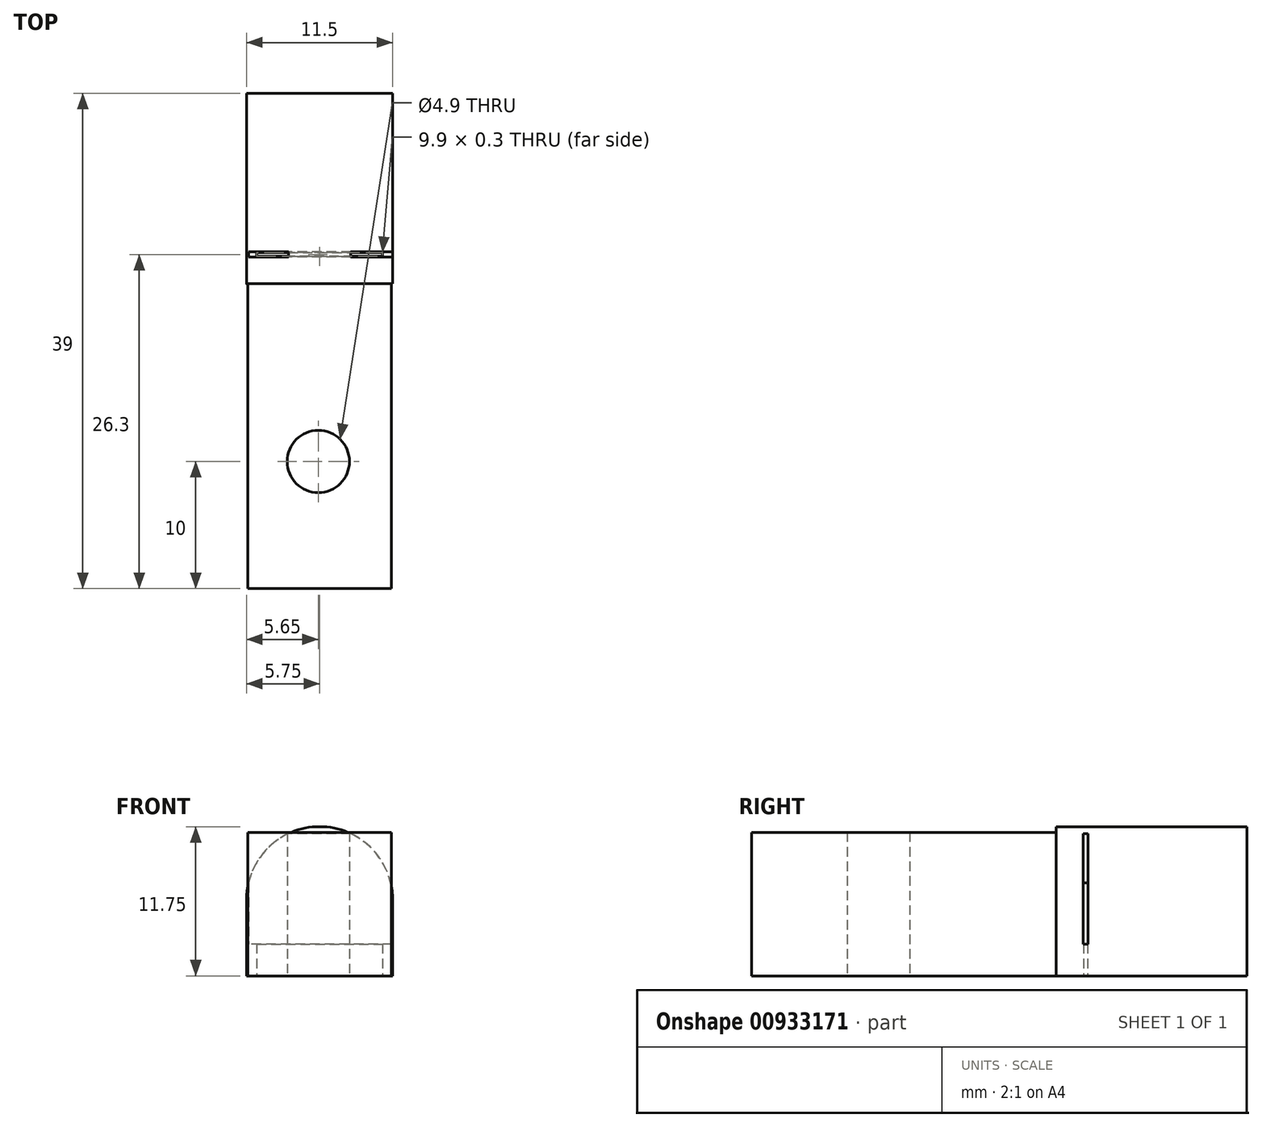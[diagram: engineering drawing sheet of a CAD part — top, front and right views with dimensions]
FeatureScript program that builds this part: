
annotation { "Feature Type Name" : "Feature", "Feature Type Description" : "" }
export const myFeature = defineFeature(function(context is Context, id is Id, definition is map)
    precondition{}
    {
        {
            var Q0;
            Q0=qCreatedBy(makeId("Front.planeOp"),FACE);
            var sketch = newSketch(context, id + "F0", { "sketchPlane" : qUnion([Q0])});
            skLineSegment(sketch, "E0.bottom", {"start": v(0, 0) * mm, "end": v(11.5, 0) * mm});
            skLineSegment(sketch, "E0.top", {"start": v(0, 6) * mm, "end": v(11.5, 6) * mm});
            skLineSegment(sketch, "E0.left", {"start": v(0, 0) * mm, "end": v(0, 6) * mm});
            skLineSegment(sketch, "E0.right", {"start": v(11.5, 0) * mm, "end": v(11.5, 6) * mm});
            skArc(sketch, "E1", {"start": v(0, 6) * mm, "mid": v(5.75, 11.75) * mm, "end": v(11.5, 6) * mm});
            skSolve(sketch);
        }
        {
            var Q0;
            Q0=makeQuery(id+"F0.imprint","IMPRINT",FACE,{"disambiguationData":[TD([[makeQuery(id+"F0.imprint","IMPRINT",EDGE,{"derivedFrom":sQuery(id+"F0.wireOp",EDGE,"E0.top")}),1.0]])]});
            var Q1;
            Q1=makeQuery(id+"F0.imprint","IMPRINT",FACE,{"disambiguationData":[TD([[makeQuery(id+"F0.imprint","IMPRINT",EDGE,{"derivedFrom":sQuery(id+"F0.wireOp",EDGE,"E0.bottom")}),1.0]])]});
            extrude(context, id + "F1", {"entities" : qUnion([Q0, Q1]), "depth" : 15 * mm, "offsetDistance" : 25 * mm});
        }
        {
            var Q0;
            Q0=makeQuery(id+"F1.opExtrude","CAP_FACE",FACE,{"disambiguationData":[OSD([sQuery(id+"F0.wireOp",EDGE,"E0.bottom"),sQuery(id+"F0.wireOp",EDGE,"E0.left"),sQuery(id+"F0.wireOp",EDGE,"E0.right"),sQuery(id+"F0.wireOp",EDGE,"E1")])],"isStart":false});
            var sketch = newSketch(context, id + "F2", { "sketchPlane" : qUnion([Q0])});
            skLineSegment(sketch, "E2.bottom", {"start": v(11.4, 0) * mm, "end": v(0.1, 0) * mm});
            skLineSegment(sketch, "E2.top", {"start": v(11.4, 11.3) * mm, "end": v(0.1, 11.3) * mm});
            skLineSegment(sketch, "E2.left", {"start": v(11.4, 0) * mm, "end": v(11.4, 11.3) * mm});
            skLineSegment(sketch, "E2.right", {"start": v(0.1, 0) * mm, "end": v(0.1, 11.3) * mm});
            skPoint(sketch, "E2.middle", {"position": v(5.75, 5.65) * mm});
            skPoint(sketch, "E2.middle.positionSnap0", {"position": v(5.75, 0) * mm});
            skPoint(sketch, "E2.centerSnap0", {"position": v(5.75, 0) * mm});
            skSolve(sketch);
        }
        {
            var Q0;
            Q0=qSketchRegion(id+"F2",true);
            extrude(context, id + "F3", {"entities" : qUnion([Q0]), "operationType" : NewBodyOperationType.ADD, "depth" : 24 * mm, "offsetDistance" : 25 * mm});
        }
        {
            var Q0;
            Q0=makeQuery(id+"F1.opExtrude","CAP_VERTEX",VERTEX,{"disambiguationData":[OSD([sQuery(id+"F0.wireOp",EDGE,"E0.top"),sQuery(id+"F0.wireOp",EDGE,"E0.left"),sQuery(id+"F0.wireOp",EDGE,"E1")])],"isStart":true});
            var Q1;
            Q1=makeQuery(id+"F1.opExtrude","CAP_VERTEX",VERTEX,{"disambiguationData":[OSD([sQuery(id+"F0.wireOp",EDGE,"E0.top"),sQuery(id+"F0.wireOp",EDGE,"E0.left"),sQuery(id+"F0.wireOp",EDGE,"E1")])],"isStart":false});
            var Q2;
            Q2=makeQuery(id+"F1.opExtrude","CAP_VERTEX",VERTEX,{"disambiguationData":[OSD([sQuery(id+"F0.wireOp",EDGE,"E0.top"),sQuery(id+"F0.wireOp",EDGE,"E0.right"),sQuery(id+"F0.wireOp",EDGE,"E1")])],"isStart":true});
            cPlane(context, id + "F4", {"entities" : qUnion([Q0, Q1, Q2]), "cplaneType" : CPlaneType.THREE_POINT, "offset" : 25 * mm, "width" : 150 * mm, "height" : 150 * mm});
        }
        {
            var Q0;
            Q0=qCreatedBy(id+"F4.planeOp",FACE);
            var sketch = newSketch(context, id + "F5", { "sketchPlane" : qUnion([Q0])});
            skPoint(sketch, "E3.0", {"position": v(11.9, 12.7) * mm});
            skPoint(sketch, "E4.0", {"position": v(0, 9.7) * mm});
            skLineSegment(sketch, "E5", {"start": v(13.51, 12.7) * mm, "end": v(-0.54, 12.7) * mm, "construction": true});
            skLineSegment(sketch, "E6.bottom", {"start": v(12.82, 12.9) * mm, "end": v(0.15, 12.9) * mm});
            skLineSegment(sketch, "E6.top", {"start": v(12.82, 12.5) * mm, "end": v(0.15, 12.5) * mm});
            skLineSegment(sketch, "E6.left", {"start": v(12.82, 12.9) * mm, "end": v(12.82, 12.5) * mm});
            skLineSegment(sketch, "E6.right", {"start": v(0.15, 12.9) * mm, "end": v(0.15, 12.5) * mm});
            skPoint(sketch, "E6.middle", {"position": v(6.49, 12.7) * mm});
            skSolve(sketch);
        }
        {
            var Q0;
            Q0=makeQuery(id+"F5.imprint","IMPRINT",FACE,{"disambiguationData":[TD([[makeQuery(id+"F5.imprint","IMPRINT",EDGE,{"derivedFrom":sQuery(id+"F5.wireOp",EDGE,"E6.bottom")}),1.0]])]});
            extrude(context, id + "F6", {"entities" : qUnion([Q0]), "operationType" : NewBodyOperationType.REMOVE, "oppositeDirection" : true, "depth" : 5.2 * mm, "offsetDistance" : 25 * mm});
        }
        {
            var Q0;
            Q0=makeQuery(id+"F3.boolean.opBoolean","MERGE",FACE,{"derivedFrom":[makeQuery(id+"F1.opExtrude","SWEPT_FACE",FACE,{"disambiguationData":[OSD([sQuery(id+"F0.wireOp",EDGE,"E0.bottom")])]}),makeQuery(id+"F3.opExtrude","SWEPT_FACE",FACE,{"disambiguationData":[OSD([sQuery(id+"F2.wireOp",EDGE,"E2.bottom")])]})]});
            var sketch = newSketch(context, id + "F7", { "sketchPlane" : qUnion([Q0])});
            skLineSegment(sketch, "E7", {"start": v(11.5, 12.7) * mm, "end": v(0, 12.7) * mm, "construction": true});
            skPoint(sketch, "E8", {"position": v(5.75, 12.7) * mm});
            skLineSegment(sketch, "E9.bottom", {"start": v(10.7, 12.55) * mm, "end": v(0.8, 12.55) * mm});
            skLineSegment(sketch, "E9.top", {"start": v(10.7, 12.85) * mm, "end": v(0.8, 12.85) * mm});
            skLineSegment(sketch, "E9.left", {"start": v(10.7, 12.55) * mm, "end": v(10.7, 12.85) * mm});
            skLineSegment(sketch, "E9.right", {"start": v(0.8, 12.55) * mm, "end": v(0.8, 12.85) * mm});
            skPoint(sketch, "E10", {"position": v(5.65, 29) * mm});
            skPoint(sketch, "E10.positionSnap0", {"position": v(5.65, 15) * mm});
            skSolve(sketch);
        }
        {
            var Q0;
            Q0=makeQuery(id+"F7.imprint","IMPRINT",FACE,{"disambiguationData":[TD([[makeQuery(id+"F7.imprint","IMPRINT",EDGE,{"derivedFrom":sQuery(id+"F7.wireOp",EDGE,"E9.bottom")}),-1.0]])]});
            var Q1;
            Q1=makeQuery(id+"F6.boolean.opBoolean","COPY",FACE,{"derivedFrom":makeQuery(id+"F6.opExtrude","CAP_FACE",FACE,{"disambiguationData":[OSD([sQuery(id+"F5.wireOp",EDGE,"E6.bottom"),sQuery(id+"F5.wireOp",EDGE,"E6.top"),sQuery(id+"F5.wireOp",EDGE,"E6.left"),sQuery(id+"F5.wireOp",EDGE,"E6.right")])],"isStart":true})});
            extrude(context, id + "F8", {"entities" : qUnion([Q0]), "operationType" : NewBodyOperationType.REMOVE, "endBound" : BoundingType.UP_TO_SURFACE, "oppositeDirection" : true, "depth" : 25 * mm, "endBoundEntityFace" : qUnion([Q1]), "offsetDistance" : 25 * mm});
        }
        {
            var Q0;
            Q0=sQuery(id+"F7.wireOp",VERTEX,"E10");
            var Q1;
            Q1=makeQuery(id+"F1.opExtrude","SWEPT_BODY",BODY,{"disambiguationData":[OSD([sQuery(id+"F0.wireOp",EDGE,"E0.bottom"),sQuery(id+"F0.wireOp",EDGE,"E0.left"),sQuery(id+"F0.wireOp",EDGE,"E0.right"),sQuery(id+"F0.wireOp",EDGE,"E1")])]});
            hole(context, id + "F9", {"style" : HoleStyle.SIMPLE, "endStyle" : HoleEndStyle.THROUGH, "holeDiameter" : 4.9 * mm, "majorDiameter" : 5 * mm, "isTappedThrough" : true, "tappedDepth" : 12 * mm, "tapClearance" : 3, "locations" : qUnion([Q0]), "scope" : qUnion([Q1])});
        }
        {
            var Q0;
            Q0=qSketchRegion(id+"F5",true);
            extrude(context, id + "F10", {"entities" : qUnion([Q0]), "operationType" : NewBodyOperationType.REMOVE, "depth" : 3.5 * mm, "offsetDistance" : 25 * mm});
        }
    });
